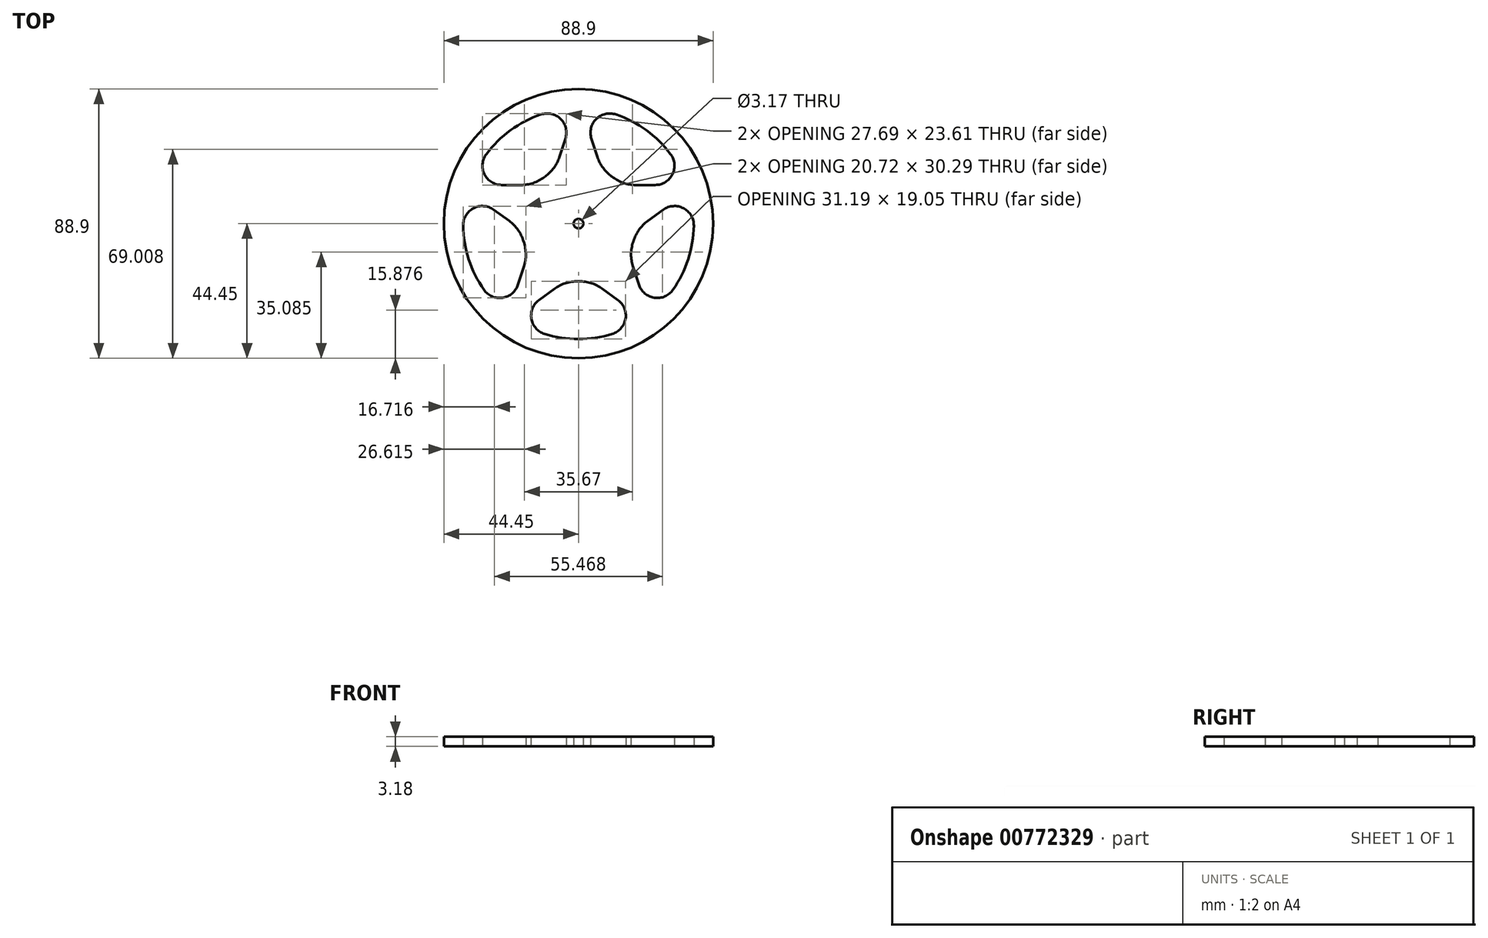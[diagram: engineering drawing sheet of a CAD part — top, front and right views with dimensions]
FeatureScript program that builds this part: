
annotation { "Feature Type Name" : "Feature", "Feature Type Description" : "" }
export const myFeature = defineFeature(function(context is Context, id is Id, definition is map)
    precondition{}
    {
        {
            var Q0;
            Q0=qCreatedBy(makeId("Top.planeOp"),FACE);
            var sketch = newSketch(context, id + "F0", { "sketchPlane" : qUnion([Q0])});
            skCircle(sketch, "E0", {"center": v(0, 0) * mm, "radius": 41.28 * mm});
            skCircle(sketch, "E1", {"center": v(0, 0) * mm, "radius": 1.59 * mm});
            skCircle(sketch, "E2", {"center": v(0, 0) * mm, "radius": 19.05 * mm});
            skCircle(sketch, "E3", {"center": v(0, 0) * mm, "radius": 38.1 * mm});
            skLineSegment(sketch, "E4", {"start": v(0, 0) * mm, "end": v(0, 41.28) * mm, "construction": true});
            skPoint(sketch, "E5.orphan", {"position": v(0, 19.05) * mm});
            skLineSegment(sketch, "E6", {"start": v(0, 0) * mm, "end": v(39.25, 12.75) * mm, "construction": true});
            skLineSegment(sketch, "E7", {"start": v(0, 0) * mm, "end": v(24.26, -33.4) * mm, "construction": true});
            skLineSegment(sketch, "E8", {"start": v(0, 0) * mm, "end": v(-39.25, 12.75) * mm, "construction": true});
            skLineSegment(sketch, "E9", {"start": v(0, 0) * mm, "end": v(-24.26, -33.4) * mm, "construction": true});
            skLineSegment(sketch, "E10", {"start": v(-22.35, -30.65) * mm, "end": v(-22.27, -30.65) * mm});
            skLineSegment(sketch, "E11", {"start": v(-39.25, 12.75) * mm, "end": v(-14.15, 12.75) * mm});
            skLineSegment(sketch, "E12", {"start": v(39.25, 12.75) * mm, "end": v(18.94, -2) * mm});
            skLineSegment(sketch, "E13", {"start": v(-24.26, -33.4) * mm, "end": v(-16.5, -9.52) * mm});
            skLineSegment(sketch, "E14", {"start": v(0, 41.28) * mm, "end": v(7.76, 17.4) * mm});
            skLineSegment(sketch, "E15", {"start": v(24.26, -33.4) * mm, "end": v(3.95, -18.64) * mm});
            skLineSegment(sketch, "E16.trimOffspring", {"start": v(14.15, 12.75) * mm, "end": v(39.25, 12.75) * mm});
            skLineSegment(sketch, "E17.trimOffspring", {"start": v(-7.76, 17.4) * mm, "end": v(0, 41.28) * mm});
            skLineSegment(sketch, "E18.trimOffspring", {"start": v(-18.94, -2) * mm, "end": v(-39.25, 12.75) * mm});
            skLineSegment(sketch, "E19.trimOffspring", {"start": v(-3.95, -18.64) * mm, "end": v(-24.26, -33.4) * mm});
            skLineSegment(sketch, "E20.trimOffspring", {"start": v(16.5, -9.52) * mm, "end": v(24.26, -33.4) * mm});
            skCircle(sketch, "E21", {"center": v(0, 0) * mm, "radius": 44.45 * mm});
            skSolve(sketch);
        }
        {
            var Q0;
            Q0=makeQuery(id+"F0.imprint","IMPRINT",FACE,{"disambiguationData":[TD([[makeQuery(id+"F0.imprint","IMPRINT",EDGE,{"derivedFrom":sQuery(id+"F0.wireOp",EDGE,"E21")}),1.0]])]});
            var Q1;
            {var subQ3=sQuery(id+"F0.wireOp",EDGE,"E17.trimOffspring");var subQ5=sQuery(id+"F0.wireOp",EDGE,"E3");var subQ7=makeQuery(id+"F0.imprint","INTERSECT",VERTEX,{"derivedFrom":[subQ5,subQ3]});Q1=makeQuery(id+"F0.imprint","IMPRINT",FACE,{"disambiguationData":[TD([[makeQuery(id+"F0.imprint","IMPRINT",EDGE,{"disambiguationData":[TD([[subQ7,-1.0]])],"derivedFrom":subQ5}),-1.0]])]});}
            var Q2;
            {var subQ0=sQuery(id+"F0.wireOp",EDGE,"E18.trimOffspring");var subQ5=sQuery(id+"F0.wireOp",EDGE,"E3");var subQ6=makeQuery(id+"F0.imprint","INTERSECT",VERTEX,{"derivedFrom":[subQ5,subQ0]});Q2=makeQuery(id+"F0.imprint","IMPRINT",FACE,{"disambiguationData":[TD([[makeQuery(id+"F0.imprint","IMPRINT",EDGE,{"disambiguationData":[TD([[subQ6,-1.0]])],"derivedFrom":subQ5}),-1.0]])]});}
            var Q3;
            {var subQ0=sQuery(id+"F0.wireOp",EDGE,"E19.trimOffspring");var subQ5=sQuery(id+"F0.wireOp",EDGE,"E3");var subQ6=makeQuery(id+"F0.imprint","INTERSECT",VERTEX,{"derivedFrom":[subQ5,subQ0]});Q3=makeQuery(id+"F0.imprint","IMPRINT",FACE,{"disambiguationData":[TD([[makeQuery(id+"F0.imprint","IMPRINT",EDGE,{"disambiguationData":[TD([[subQ6,-1.0]])],"derivedFrom":subQ5}),-1.0]])]});}
            var Q4;
            {var subQ0=sQuery(id+"F0.wireOp",EDGE,"E12");var subQ5=sQuery(id+"F0.wireOp",EDGE,"E3");var subQ6=makeQuery(id+"F0.imprint","INTERSECT",VERTEX,{"derivedFrom":[subQ5,subQ0]});Q4=makeQuery(id+"F0.imprint","IMPRINT",FACE,{"disambiguationData":[TD([[makeQuery(id+"F0.imprint","IMPRINT",EDGE,{"disambiguationData":[TD([[subQ6,1.0]])],"derivedFrom":subQ5}),-1.0]])]});}
            var Q5;
            {var subQ0=sQuery(id+"F0.wireOp",EDGE,"E16.trimOffspring");var subQ5=sQuery(id+"F0.wireOp",EDGE,"E3");var subQ6=makeQuery(id+"F0.imprint","INTERSECT",VERTEX,{"derivedFrom":[subQ5,subQ0]});Q5=makeQuery(id+"F0.imprint","IMPRINT",FACE,{"disambiguationData":[TD([[makeQuery(id+"F0.imprint","IMPRINT",EDGE,{"disambiguationData":[TD([[subQ6,-1.0]])],"derivedFrom":subQ5}),-1.0]])]});}
            var Q6;
            {var subQ0=sQuery(id+"F0.wireOp",EDGE,"E14");var subQ1=sQuery(id+"F0.wireOp",EDGE,"E2");var subQ2=makeQuery(id+"F0.imprint","INTERSECT",VERTEX,{"derivedFrom":[subQ1,subQ0]});Q6=makeQuery(id+"F0.imprint","IMPRINT",FACE,{"disambiguationData":[TD([[makeQuery(id+"F0.imprint","IMPRINT",EDGE,{"disambiguationData":[TD([[subQ2,-1.0]])],"derivedFrom":subQ1}),-1.0]])]});}
            var Q7;
            {var subQ0=sQuery(id+"F0.wireOp",EDGE,"E11");var subQ1=sQuery(id+"F0.wireOp",EDGE,"E2");var subQ2=makeQuery(id+"F0.imprint","INTERSECT",VERTEX,{"derivedFrom":[subQ1,subQ0]});Q7=makeQuery(id+"F0.imprint","IMPRINT",FACE,{"disambiguationData":[TD([[makeQuery(id+"F0.imprint","IMPRINT",EDGE,{"disambiguationData":[TD([[subQ2,-1.0]])],"derivedFrom":subQ1}),-1.0]])]});}
            var Q8;
            {var subQ0=sQuery(id+"F0.wireOp",EDGE,"E12");var subQ1=sQuery(id+"F0.wireOp",EDGE,"E2");var subQ2=makeQuery(id+"F0.imprint","INTERSECT",VERTEX,{"derivedFrom":[subQ1,subQ0]});Q8=makeQuery(id+"F0.imprint","IMPRINT",FACE,{"disambiguationData":[TD([[makeQuery(id+"F0.imprint","IMPRINT",EDGE,{"disambiguationData":[TD([[subQ2,-1.0]])],"derivedFrom":subQ1}),-1.0]])]});}
            var Q9;
            {var subQ0=sQuery(id+"F0.wireOp",EDGE,"E15");var subQ1=sQuery(id+"F0.wireOp",EDGE,"E2");var subQ2=makeQuery(id+"F0.imprint","INTERSECT",VERTEX,{"derivedFrom":[subQ1,subQ0]});Q9=makeQuery(id+"F0.imprint","IMPRINT",FACE,{"disambiguationData":[TD([[makeQuery(id+"F0.imprint","IMPRINT",EDGE,{"disambiguationData":[TD([[subQ2,-1.0]])],"derivedFrom":subQ1}),-1.0]])]});}
            var Q10;
            {var subQ0=sQuery(id+"F0.wireOp",EDGE,"E13");var subQ1=sQuery(id+"F0.wireOp",EDGE,"E2");var subQ2=makeQuery(id+"F0.imprint","INTERSECT",VERTEX,{"derivedFrom":[subQ1,subQ0]});Q10=makeQuery(id+"F0.imprint","IMPRINT",FACE,{"disambiguationData":[TD([[makeQuery(id+"F0.imprint","IMPRINT",EDGE,{"disambiguationData":[TD([[subQ2,-1.0]])],"derivedFrom":subQ1}),-1.0]])]});}
            var Q11;
            {var subQ0=sQuery(id+"F0.wireOp",EDGE,"E11");var subQ1=sQuery(id+"F0.wireOp",EDGE,"E3");var subQ2=makeQuery(id+"F0.imprint","INTERSECT",VERTEX,{"derivedFrom":[subQ1,subQ0]});Q11=makeQuery(id+"F0.imprint","IMPRINT",FACE,{"disambiguationData":[TD([[makeQuery(id+"F0.imprint","IMPRINT",EDGE,{"disambiguationData":[TD([[subQ2,-1.0]])],"derivedFrom":subQ1}),-1.0]])]});}
            var Q12;
            {var subQ0=sQuery(id+"F0.wireOp",EDGE,"E13");var subQ1=sQuery(id+"F0.wireOp",EDGE,"E3");var subQ2=makeQuery(id+"F0.imprint","INTERSECT",VERTEX,{"derivedFrom":[subQ1,subQ0]});Q12=makeQuery(id+"F0.imprint","IMPRINT",FACE,{"disambiguationData":[TD([[makeQuery(id+"F0.imprint","IMPRINT",EDGE,{"disambiguationData":[TD([[subQ2,-1.0]])],"derivedFrom":subQ1}),-1.0]])]});}
            var Q13;
            {var subQ0=sQuery(id+"F0.wireOp",EDGE,"E15");var subQ1=sQuery(id+"F0.wireOp",EDGE,"E3");var subQ2=makeQuery(id+"F0.imprint","INTERSECT",VERTEX,{"derivedFrom":[subQ1,subQ0]});Q13=makeQuery(id+"F0.imprint","IMPRINT",FACE,{"disambiguationData":[TD([[makeQuery(id+"F0.imprint","IMPRINT",EDGE,{"disambiguationData":[TD([[subQ2,-1.0]])],"derivedFrom":subQ1}),-1.0]])]});}
            var Q14;
            {var subQ0=sQuery(id+"F0.wireOp",EDGE,"E16.trimOffspring");var subQ1=sQuery(id+"F0.wireOp",EDGE,"E3");var subQ2=makeQuery(id+"F0.imprint","INTERSECT",VERTEX,{"derivedFrom":[subQ1,subQ0]});Q14=makeQuery(id+"F0.imprint","IMPRINT",FACE,{"disambiguationData":[TD([[makeQuery(id+"F0.imprint","IMPRINT",EDGE,{"disambiguationData":[TD([[subQ2,1.0]])],"derivedFrom":subQ1}),-1.0]])]});}
            var Q15;
            {var subQ0=sQuery(id+"F0.wireOp",EDGE,"E14");var subQ1=sQuery(id+"F0.wireOp",EDGE,"E3");var subQ2=makeQuery(id+"F0.imprint","INTERSECT",VERTEX,{"derivedFrom":[subQ1,subQ0]});Q15=makeQuery(id+"F0.imprint","IMPRINT",FACE,{"disambiguationData":[TD([[makeQuery(id+"F0.imprint","IMPRINT",EDGE,{"disambiguationData":[TD([[subQ2,-1.0]])],"derivedFrom":subQ1}),-1.0]])]});}
            var Q16;
            Q16=makeQuery(id+"F0.imprint","IMPRINT",FACE,{"disambiguationData":[TD([[makeQuery(id+"F0.imprint","IMPRINT",EDGE,{"derivedFrom":sQuery(id+"F0.wireOp",EDGE,"E1")}),-1.0]])]});
            extrude(context, id + "F1", {"entities" : qUnion([Q0, Q1, Q2, Q3, Q4, Q5, Q6, Q7, Q8, Q9, Q10, Q11, Q12, Q13, Q14, Q15, Q16]), "depth" : 3.17 * mm, "offsetDistance" : 25.4 * mm});
        }
        {
            var Q0;
            Q0=makeQuery(id+"F1.opExtrude","SWEPT_EDGE",EDGE,{"disambiguationData":[OSD([sQuery(id+"F0.wireOp",EDGE,"E2"),sQuery(id+"F0.wireOp",EDGE,"E17.trimOffspring")])]});
            var Q1;
            Q1=makeQuery(id+"F1.opExtrude","SWEPT_EDGE",EDGE,{"disambiguationData":[OSD([sQuery(id+"F0.wireOp",EDGE,"E2"),sQuery(id+"F0.wireOp",EDGE,"E14")])]});
            var Q2;
            Q2=makeQuery(id+"F1.opExtrude","SWEPT_EDGE",EDGE,{"disambiguationData":[OSD([sQuery(id+"F0.wireOp",EDGE,"E2"),sQuery(id+"F0.wireOp",EDGE,"E20.trimOffspring")])]});
            var Q3;
            Q3=makeQuery(id+"F1.opExtrude","SWEPT_EDGE",EDGE,{"disambiguationData":[OSD([sQuery(id+"F0.wireOp",EDGE,"E2"),sQuery(id+"F0.wireOp",EDGE,"E12")])]});
            var Q4;
            Q4=makeQuery(id+"F1.opExtrude","SWEPT_EDGE",EDGE,{"disambiguationData":[OSD([sQuery(id+"F0.wireOp",EDGE,"E2"),sQuery(id+"F0.wireOp",EDGE,"E16.trimOffspring")])]});
            var Q5;
            Q5=makeQuery(id+"F1.opExtrude","SWEPT_EDGE",EDGE,{"disambiguationData":[OSD([sQuery(id+"F0.wireOp",EDGE,"E2"),sQuery(id+"F0.wireOp",EDGE,"E11")])]});
            var Q6;
            Q6=makeQuery(id+"F1.opExtrude","SWEPT_EDGE",EDGE,{"disambiguationData":[OSD([sQuery(id+"F0.wireOp",EDGE,"E2"),sQuery(id+"F0.wireOp",EDGE,"E13")])]});
            var Q7;
            Q7=makeQuery(id+"F1.opExtrude","SWEPT_EDGE",EDGE,{"disambiguationData":[OSD([sQuery(id+"F0.wireOp",EDGE,"E2"),sQuery(id+"F0.wireOp",EDGE,"E18.trimOffspring")])]});
            var Q8;
            Q8=makeQuery(id+"F1.opExtrude","SWEPT_EDGE",EDGE,{"disambiguationData":[OSD([sQuery(id+"F0.wireOp",EDGE,"E2"),sQuery(id+"F0.wireOp",EDGE,"E19.trimOffspring")])]});
            var Q9;
            Q9=makeQuery(id+"F1.opExtrude","SWEPT_EDGE",EDGE,{"disambiguationData":[OSD([sQuery(id+"F0.wireOp",EDGE,"E2"),sQuery(id+"F0.wireOp",EDGE,"E15")])]});
            fillet(context, id + "F2", {"entities" : qUnion([Q0, Q1, Q2, Q3, Q4, Q5, Q6, Q7, Q8, Q9]), "radius" : 12.7 * mm, "tangentPropagation" : true, "allowEdgeOverflow" : false});
        }
        {
            var Q0;
            Q0=makeQuery(id+"F1.opExtrude","SWEPT_EDGE",EDGE,{"disambiguationData":[OSD([sQuery(id+"F0.wireOp",EDGE,"E3"),sQuery(id+"F0.wireOp",EDGE,"E19.trimOffspring")])]});
            var Q1;
            Q1=makeQuery(id+"F1.opExtrude","SWEPT_EDGE",EDGE,{"disambiguationData":[OSD([sQuery(id+"F0.wireOp",EDGE,"E3"),sQuery(id+"F0.wireOp",EDGE,"E15")])]});
            var Q2;
            Q2=makeQuery(id+"F1.opExtrude","SWEPT_EDGE",EDGE,{"disambiguationData":[OSD([sQuery(id+"F0.wireOp",EDGE,"E3"),sQuery(id+"F0.wireOp",EDGE,"E18.trimOffspring")])]});
            var Q3;
            Q3=makeQuery(id+"F1.opExtrude","SWEPT_EDGE",EDGE,{"disambiguationData":[OSD([sQuery(id+"F0.wireOp",EDGE,"E3"),sQuery(id+"F0.wireOp",EDGE,"E13")])]});
            var Q4;
            Q4=makeQuery(id+"F1.opExtrude","SWEPT_EDGE",EDGE,{"disambiguationData":[OSD([sQuery(id+"F0.wireOp",EDGE,"E3"),sQuery(id+"F0.wireOp",EDGE,"E11")])]});
            var Q5;
            Q5=makeQuery(id+"F1.opExtrude","SWEPT_EDGE",EDGE,{"disambiguationData":[OSD([sQuery(id+"F0.wireOp",EDGE,"E3"),sQuery(id+"F0.wireOp",EDGE,"E14")])]});
            var Q6;
            Q6=makeQuery(id+"F1.opExtrude","SWEPT_EDGE",EDGE,{"disambiguationData":[OSD([sQuery(id+"F0.wireOp",EDGE,"E3"),sQuery(id+"F0.wireOp",EDGE,"E20.trimOffspring")])]});
            var Q7;
            Q7=makeQuery(id+"F1.opExtrude","SWEPT_EDGE",EDGE,{"disambiguationData":[OSD([sQuery(id+"F0.wireOp",EDGE,"E3"),sQuery(id+"F0.wireOp",EDGE,"E17.trimOffspring")])]});
            var Q8;
            Q8=makeQuery(id+"F1.opExtrude","SWEPT_EDGE",EDGE,{"disambiguationData":[OSD([sQuery(id+"F0.wireOp",EDGE,"E3"),sQuery(id+"F0.wireOp",EDGE,"E16.trimOffspring")])]});
            var Q9;
            Q9=makeQuery(id+"F1.opExtrude","SWEPT_EDGE",EDGE,{"disambiguationData":[OSD([sQuery(id+"F0.wireOp",EDGE,"E3"),sQuery(id+"F0.wireOp",EDGE,"E12")])]});
            fillet(context, id + "F3", {"entities" : qUnion([Q0, Q1, Q2, Q3, Q4, Q5, Q6, Q7, Q8, Q9]), "radius" : 6.35 * mm, "tangentPropagation" : true, "allowEdgeOverflow" : false});
        }
    });
